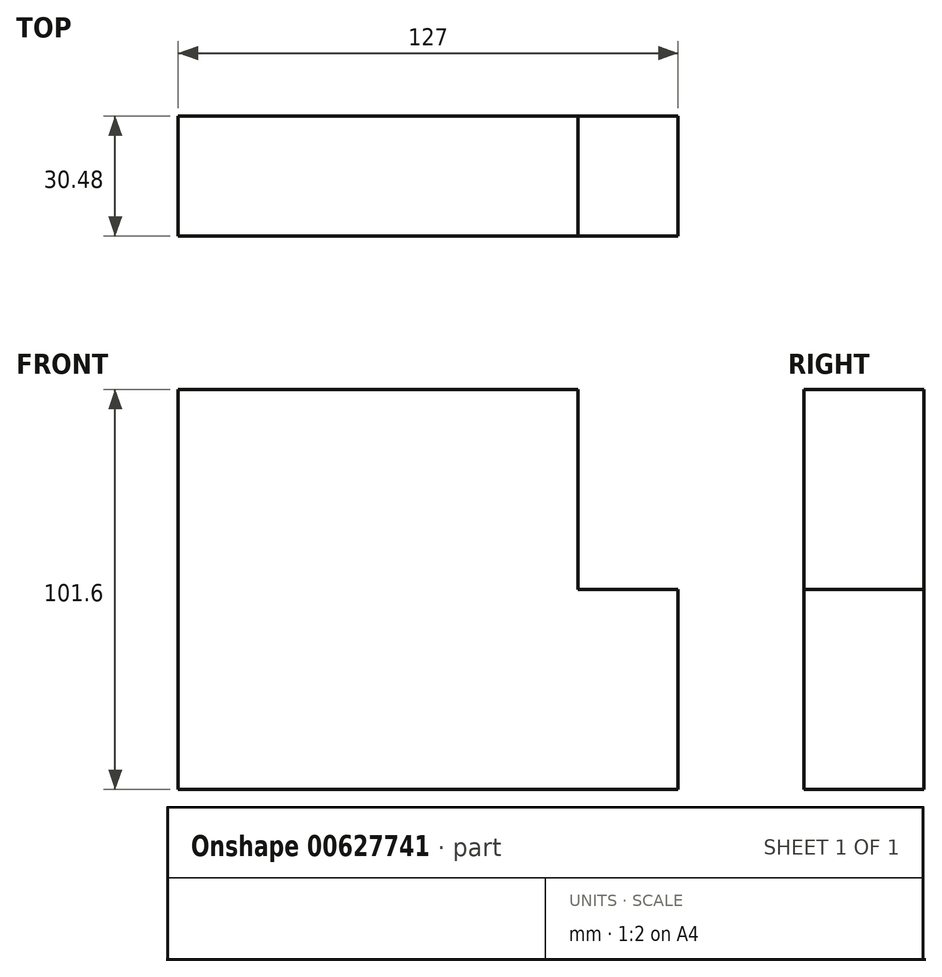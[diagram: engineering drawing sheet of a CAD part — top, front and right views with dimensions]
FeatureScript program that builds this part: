
annotation { "Feature Type Name" : "Feature", "Feature Type Description" : "" }
export const myFeature = defineFeature(function(context is Context, id is Id, definition is map)
    precondition{}
    {
        {
            var Q0;
            Q0=qCreatedBy(makeId("Front.planeOp"),FACE);
            var sketch = newSketch(context, id + "F0", { "sketchPlane" : qUnion([Q0])});
            skLineSegment(sketch, "E0", {"start": v(-47.76, 34.18) * mm, "end": v(-47.76, -67.42) * mm});
            skLineSegment(sketch, "E1", {"start": v(-47.76, -67.42) * mm, "end": v(79.24, -67.42) * mm});
            skLineSegment(sketch, "E2", {"start": v(79.24, -67.42) * mm, "end": v(79.24, -16.62) * mm});
            skLineSegment(sketch, "E3", {"start": v(79.24, -16.62) * mm, "end": v(53.84, -16.62) * mm});
            skLineSegment(sketch, "E4", {"start": v(53.84, -16.62) * mm, "end": v(53.84, 34.18) * mm});
            skLineSegment(sketch, "E5", {"start": v(53.84, 34.18) * mm, "end": v(-47.76, 34.18) * mm});
            skSolve(sketch);
        }
        {
            var Q0;
            Q0 = qSketchRegion(id + "F0", true);
            extrude(context, id + "F1", {"entities" : qUnion([Q0]), "depth" : 30.48 * mm, "offsetDistance" : 25.4 * mm});
        }
    });
